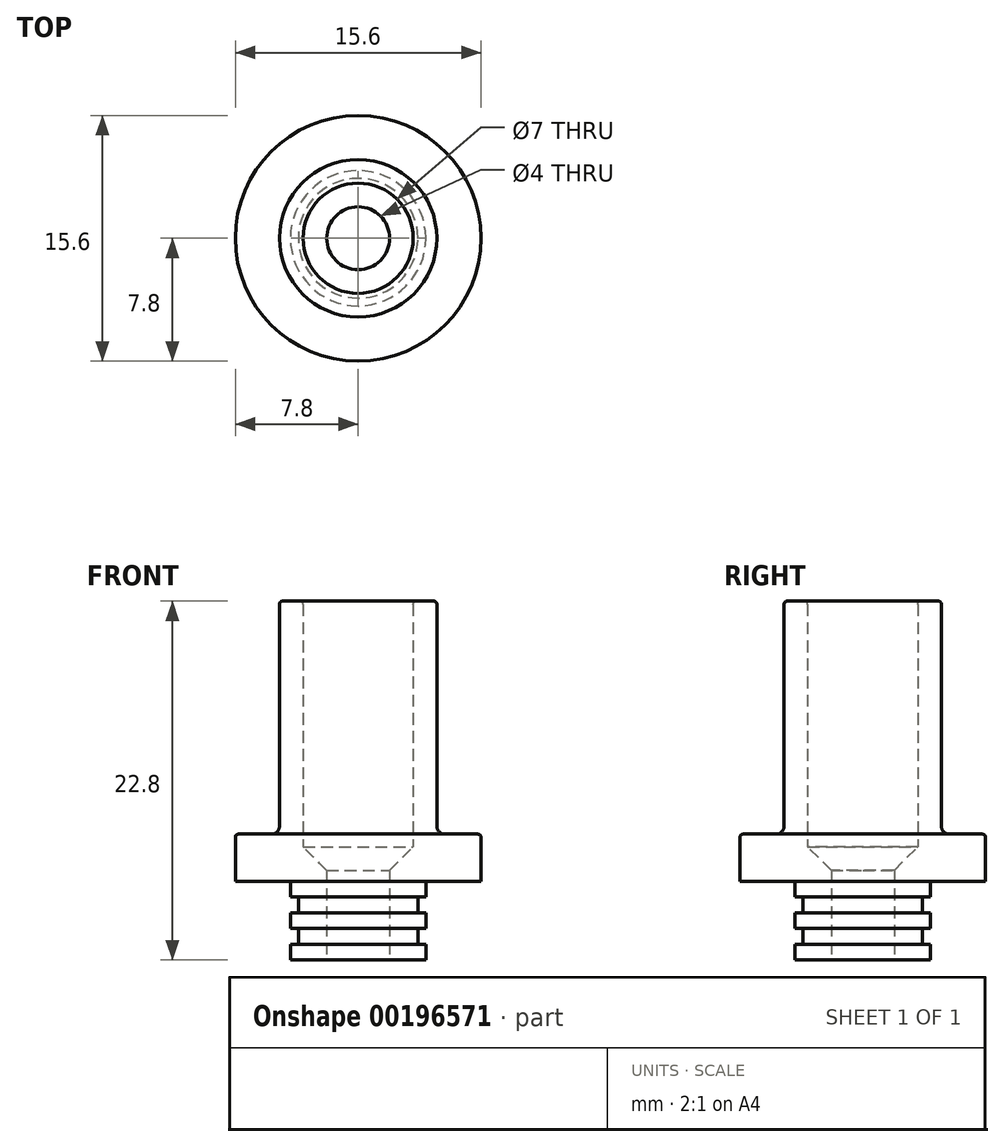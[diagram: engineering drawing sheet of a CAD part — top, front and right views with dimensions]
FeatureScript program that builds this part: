
annotation { "Feature Type Name" : "Feature", "Feature Type Description" : "" }
export const myFeature = defineFeature(function(context is Context, id is Id, definition is map)
    precondition{}
    {
        {
            var Q0;
            Q0=qCreatedBy(makeId("Front.planeOp"),FACE);
            var sketch = newSketch(context, id + "F0", { "sketchPlane" : qUnion([Q0])});
            skLineSegment(sketch, "E0", {"start": v(3.7, 22.8) * mm, "end": v(4.8, 22.8) * mm});
            skLineSegment(sketch, "E1", {"start": v(5, 22.6) * mm, "end": v(5, 8.5) * mm});
            skLineSegment(sketch, "E2", {"start": v(5.5, 8) * mm, "end": v(7.6, 8) * mm});
            skLineSegment(sketch, "E3", {"start": v(7.8, 7.8) * mm, "end": v(7.8, 5) * mm});
            skLineSegment(sketch, "E4", {"start": v(7.8, 5) * mm, "end": v(4.3, 5) * mm});
            skLineSegment(sketch, "E5", {"start": v(4.3, 5) * mm, "end": v(4.3, 4) * mm});
            skLineSegment(sketch, "E6", {"start": v(4.3, 0) * mm, "end": v(2, 0) * mm});
            skLineSegment(sketch, "E7", {"start": v(0, 0) * mm, "end": v(0, 22.8) * mm, "construction": true});
            skLineSegment(sketch, "E8", {"start": v(3.5, 22.6) * mm, "end": v(3.5, 7.2) * mm});
            skLineSegment(sketch, "E9", {"start": v(3.5, 7.2) * mm, "end": v(2, 5.7) * mm});
            skLineSegment(sketch, "E10", {"start": v(2, 5.7) * mm, "end": v(2, 0) * mm});
            skPoint(sketch, "E11.visualSharp", {"position": v(4.3, 5) * mm});
            skPoint(sketch, "E12.visualSharp", {"position": v(7.8, 5) * mm});
            skPoint(sketch, "E13.visualSharp", {"position": v(5, 22.8) * mm});
            skArc(sketch, "E13.filletArc", {"start": v(5, 22.6) * mm, "mid": v(4.94, 22.74) * mm, "end": v(4.8, 22.8) * mm});
            skPoint(sketch, "E14.visualSharp", {"position": v(3.5, 22.8) * mm});
            skArc(sketch, "E14.filletArc", {"start": v(3.7, 22.8) * mm, "mid": v(3.56, 22.74) * mm, "end": v(3.5, 22.6) * mm});
            skPoint(sketch, "E15.visualSharp", {"position": v(5, 8) * mm});
            skArc(sketch, "E15.filletArc", {"start": v(5, 8.5) * mm, "mid": v(5.15, 8.15) * mm, "end": v(5.5, 8) * mm});
            skPoint(sketch, "E16.visualSharp", {"position": v(7.8, 8) * mm});
            skArc(sketch, "E16.filletArc", {"start": v(7.8, 7.8) * mm, "mid": v(7.74, 7.94) * mm, "end": v(7.6, 8) * mm});
            skLineSegment(sketch, "E17", {"start": v(4.3, 1) * mm, "end": v(3.8, 1) * mm});
            skLineSegment(sketch, "E18", {"start": v(3.8, 1) * mm, "end": v(3.8, 2) * mm});
            skLineSegment(sketch, "E19", {"start": v(3.8, 2) * mm, "end": v(4.3, 2) * mm});
            skLineSegment(sketch, "E20", {"start": v(4.3, 3) * mm, "end": v(3.8, 3) * mm});
            skLineSegment(sketch, "E21", {"start": v(3.8, 3) * mm, "end": v(3.8, 4) * mm});
            skLineSegment(sketch, "E22", {"start": v(3.8, 4) * mm, "end": v(4.3, 4) * mm});
            skLineSegment(sketch, "E23.trimOffspring", {"start": v(4.3, 3) * mm, "end": v(4.3, 2) * mm});
            skLineSegment(sketch, "E24.trimOffspring", {"start": v(4.3, 1) * mm, "end": v(4.3, 0) * mm});
            skSolve(sketch);
        }
        {
            var Q0;
            Q0 = qSketchRegion(id + "F0", true);
            var Q1;
            Q1=sQuery(id+"F0.wireOp",EDGE,"E7");
            revolve(context, id + "F1", {"entities" : qUnion([Q0]), "axis" : qUnion([Q1]), "revolveType" : RevolveType.FULL});
        }
    });
